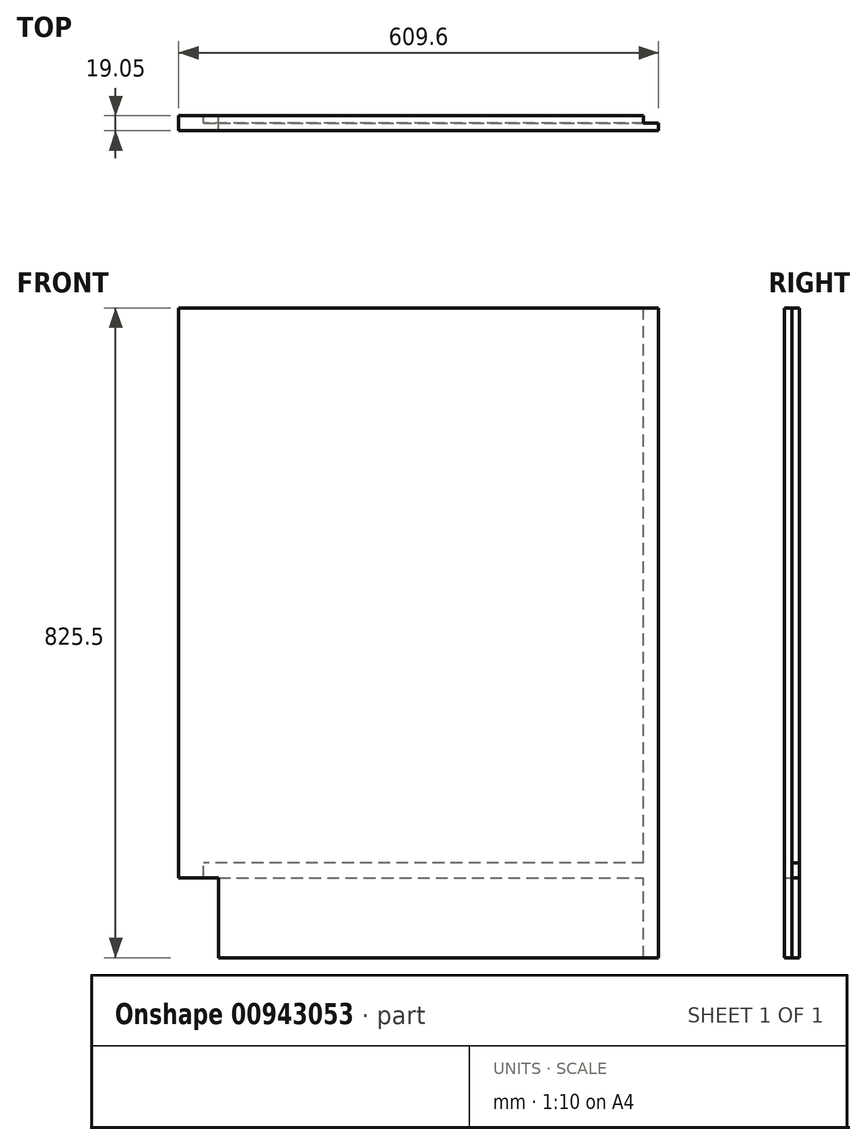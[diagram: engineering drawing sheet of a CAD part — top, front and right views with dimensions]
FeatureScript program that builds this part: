
annotation { "Feature Type Name" : "Feature", "Feature Type Description" : "" }
export const myFeature = defineFeature(function(context is Context, id is Id, definition is map)
    precondition{}
    {
        {
            var Q0;
            Q0=qCreatedBy(makeId("Front.planeOp"),FACE);
            var sketch = newSketch(context, id + "F0", { "sketchPlane" : qUnion([Q0])});
            skLineSegment(sketch, "E0.bottom", {"start": v(0, 0) * mm, "end": v(-558.8, 0) * mm});
            skLineSegment(sketch, "E0.top", {"start": v(0, 825.5) * mm, "end": v(-609.6, 825.5) * mm});
            skLineSegment(sketch, "E0.left", {"start": v(0, 0) * mm, "end": v(0, 825.5) * mm});
            skLineSegment(sketch, "E0.right", {"start": v(-609.6, 101.6) * mm, "end": v(-609.6, 825.5) * mm});
            skLineSegment(sketch, "E1", {"start": v(-609.6, 101.6) * mm, "end": v(-558.8, 101.6) * mm});
            skLineSegment(sketch, "E2", {"start": v(-558.8, 101.6) * mm, "end": v(-558.8, 0) * mm});
            skSolve(sketch);
        }
        {
            var Q0;
            Q0=makeQuery(id+"F0.imprint","IMPRINT",FACE,{"disambiguationData":[TD([[makeQuery(id+"F0.imprint","IMPRINT",EDGE,{"derivedFrom":sQuery(id+"F0.wireOp",EDGE,"E0.bottom")}),-1.0]])]});
            extrude(context, id + "F1", {"entities" : qUnion([Q0]), "depth" : 19.05 * mm, "offsetDistance" : 25.4 * mm});
        }
        {
            var Q0;
            Q0=makeQuery(id+"F1.opExtrude","CAP_FACE",FACE,{"disambiguationData":[OSD([sQuery(id+"F0.wireOp",EDGE,"E0.bottom"),sQuery(id+"F0.wireOp",EDGE,"E0.top"),sQuery(id+"F0.wireOp",EDGE,"E0.left"),sQuery(id+"F0.wireOp",EDGE,"E0.right"),sQuery(id+"F0.wireOp",EDGE,"E1"),sQuery(id+"F0.wireOp",EDGE,"E2")])],"isStart":true});
            var sketch = newSketch(context, id + "F2", { "sketchPlane" : qUnion([Q0])});
            skLineSegment(sketch, "E3", {"start": v(0, 825.5) * mm, "end": v(19.05, 825.5) * mm});
            skLineSegment(sketch, "E4", {"start": v(19.05, 0) * mm, "end": v(0, 0) * mm});
            skLineSegment(sketch, "E5", {"start": v(19.05, 0) * mm, "end": v(19.05, 101.6) * mm});
            skLineSegment(sketch, "E6", {"start": v(577.85, 101.6) * mm, "end": v(19.05, 101.6) * mm});
            skLineSegment(sketch, "E7", {"start": v(577.85, 101.6) * mm, "end": v(577.85, 120.65) * mm});
            skLineSegment(sketch, "E8", {"start": v(19.05, 120.65) * mm, "end": v(577.85, 120.65) * mm});
            skLineSegment(sketch, "E9", {"start": v(19.05, 120.65) * mm, "end": v(19.05, 825.5) * mm});
            skSolve(sketch);
        }
        {
            var Q0;
            {var subQ0=sQuery(id+"F2.wireOp",EDGE,"E6");var subQ7=makeQuery(id+"F2.imprint","INTERSECT",VERTEX,{"derivedFrom":[makeQuery(id+"F1.opExtrude","CAP_EDGE",EDGE,{"disambiguationData":[OSD([sQuery(id+"F0.wireOp",EDGE,"E2")])],"isStart":true}),subQ0]});Q0=makeQuery(id+"F2.imprint","IMPRINT",FACE,{"disambiguationData":[TD([[makeQuery(id+"F2.imprint","IMPRINT",EDGE,{"disambiguationData":[TD([[subQ7,-1.0]])],"derivedFrom":subQ0}),-1.0]])]});}
            extrude(context, id + "F3", {"entities" : qUnion([Q0]), "operationType" : NewBodyOperationType.REMOVE, "oppositeDirection" : true, "depth" : 9.52 * mm, "offsetDistance" : 25.4 * mm});
        }
    });
